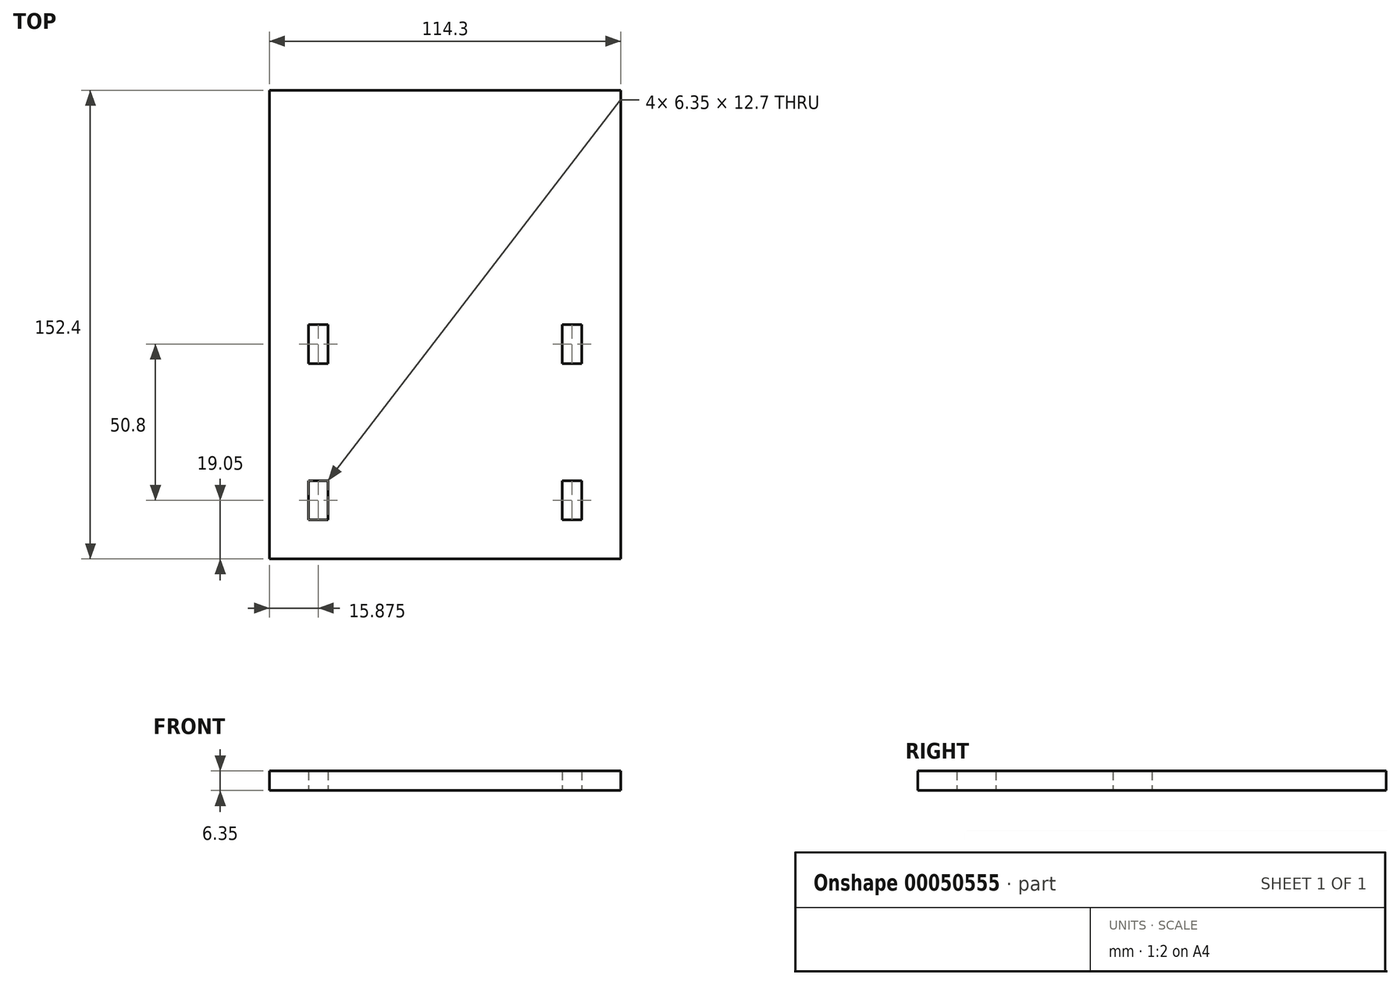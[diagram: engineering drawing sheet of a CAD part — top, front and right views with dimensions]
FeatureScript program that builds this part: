
annotation { "Feature Type Name" : "Feature", "Feature Type Description" : "" }
export const myFeature = defineFeature(function(context is Context, id is Id, definition is map)
    precondition{}
    {
        {
            var Q0;
            Q0=qCreatedBy(makeId("Top.planeOp"),FACE);
            var sketch = newSketch(context, id + "F0", { "sketchPlane" : qUnion([Q0])});
            skLineSegment(sketch, "E0.rect.bottom", {"start": v(57.15, -76.2) * mm, "end": v(-57.15, -76.2) * mm});
            skLineSegment(sketch, "E0.rect.top", {"start": v(57.15, 76.2) * mm, "end": v(-57.15, 76.2) * mm});
            skLineSegment(sketch, "E0.rect.left", {"start": v(57.15, -76.2) * mm, "end": v(57.15, 76.2) * mm});
            skLineSegment(sketch, "E0.rect.right", {"start": v(-57.15, -76.2) * mm, "end": v(-57.15, 76.2) * mm});
            skPoint(sketch, "E0.rect.middle", {"position": v(0, 0) * mm});
            skLineSegment(sketch, "E1.rect.bottom", {"start": v(-38.1, -12.7) * mm, "end": v(-44.45, -12.7) * mm});
            skLineSegment(sketch, "E1.rect.top", {"start": v(-38.1, 0) * mm, "end": v(-44.45, 0) * mm});
            skLineSegment(sketch, "E1.rect.left", {"start": v(-38.1, -12.7) * mm, "end": v(-38.1, 0) * mm});
            skLineSegment(sketch, "E1.rect.right", {"start": v(-44.45, -12.7) * mm, "end": v(-44.45, 0) * mm});
            skPoint(sketch, "E1.rect.middle", {"position": v(-41.28, -6.35) * mm});
            skLineSegment(sketch, "E2.rect.bottom", {"start": v(-38.1, -50.8) * mm, "end": v(-44.45, -50.8) * mm});
            skLineSegment(sketch, "E2.rect.top", {"start": v(-38.1, -63.5) * mm, "end": v(-44.45, -63.5) * mm});
            skLineSegment(sketch, "E2.rect.left", {"start": v(-38.1, -50.8) * mm, "end": v(-38.1, -63.5) * mm});
            skLineSegment(sketch, "E2.rect.right", {"start": v(-44.45, -50.8) * mm, "end": v(-44.45, -63.5) * mm});
            skPoint(sketch, "E2.rect.middle", {"position": v(-41.28, -57.15) * mm});
            skPoint(sketch, "E2.rect.middle.positionSnap0", {"position": v(-41.28, -12.7) * mm});
            skPoint(sketch, "E2.rect.centerSnap0", {"position": v(-41.28, -12.7) * mm});
            skLineSegment(sketch, "E3", {"start": v(-44.45, -12.7) * mm, "end": v(-44.45, -50.8) * mm, "construction": true});
            skLineSegment(sketch, "E4", {"start": v(-44.45, 0) * mm, "end": v(-57.15, 0) * mm, "construction": true});
            skLineSegment(sketch, "E5", {"start": v(0, 0) * mm, "end": v(0, -27.92) * mm, "construction": true});
            skPoint(sketch, "E6.MirrorP", {"position": v(41.28, -6.35) * mm});
            skLineSegment(sketch, "E7.MirrorCS", {"start": v(38.1, 0) * mm, "end": v(44.45, 0) * mm});
            skLineSegment(sketch, "E8.MirrorCS", {"start": v(38.1, -12.7) * mm, "end": v(38.1, 0) * mm});
            skLineSegment(sketch, "E9.MirrorCS", {"start": v(44.45, -12.7) * mm, "end": v(44.45, 0) * mm});
            skLineSegment(sketch, "E10.MirrorCS", {"start": v(38.1, -12.7) * mm, "end": v(44.45, -12.7) * mm});
            skLineSegment(sketch, "E11.MirrorCS", {"start": v(38.1, -50.8) * mm, "end": v(44.45, -50.8) * mm});
            skLineSegment(sketch, "E12.MirrorCS", {"start": v(44.45, -50.8) * mm, "end": v(44.45, -63.5) * mm});
            skLineSegment(sketch, "E13.MirrorCS", {"start": v(38.1, -50.8) * mm, "end": v(38.1, -63.5) * mm});
            skLineSegment(sketch, "E14.MirrorCS", {"start": v(38.1, -63.5) * mm, "end": v(44.45, -63.5) * mm});
            skPoint(sketch, "E15.MirrorP", {"position": v(41.28, -57.15) * mm});
            skLineSegment(sketch, "E16", {"start": v(-44.45, -63.5) * mm, "end": v(-44.45, -76.2) * mm, "construction": true});
            skSolve(sketch);
        }
        {
            var Q0;
            Q0 = qSketchRegion(id + "F0", true);
            extrude(context, id + "F1", {"entities" : qUnion([Q0]), "depth" : 6.35 * mm});
        }
    });
